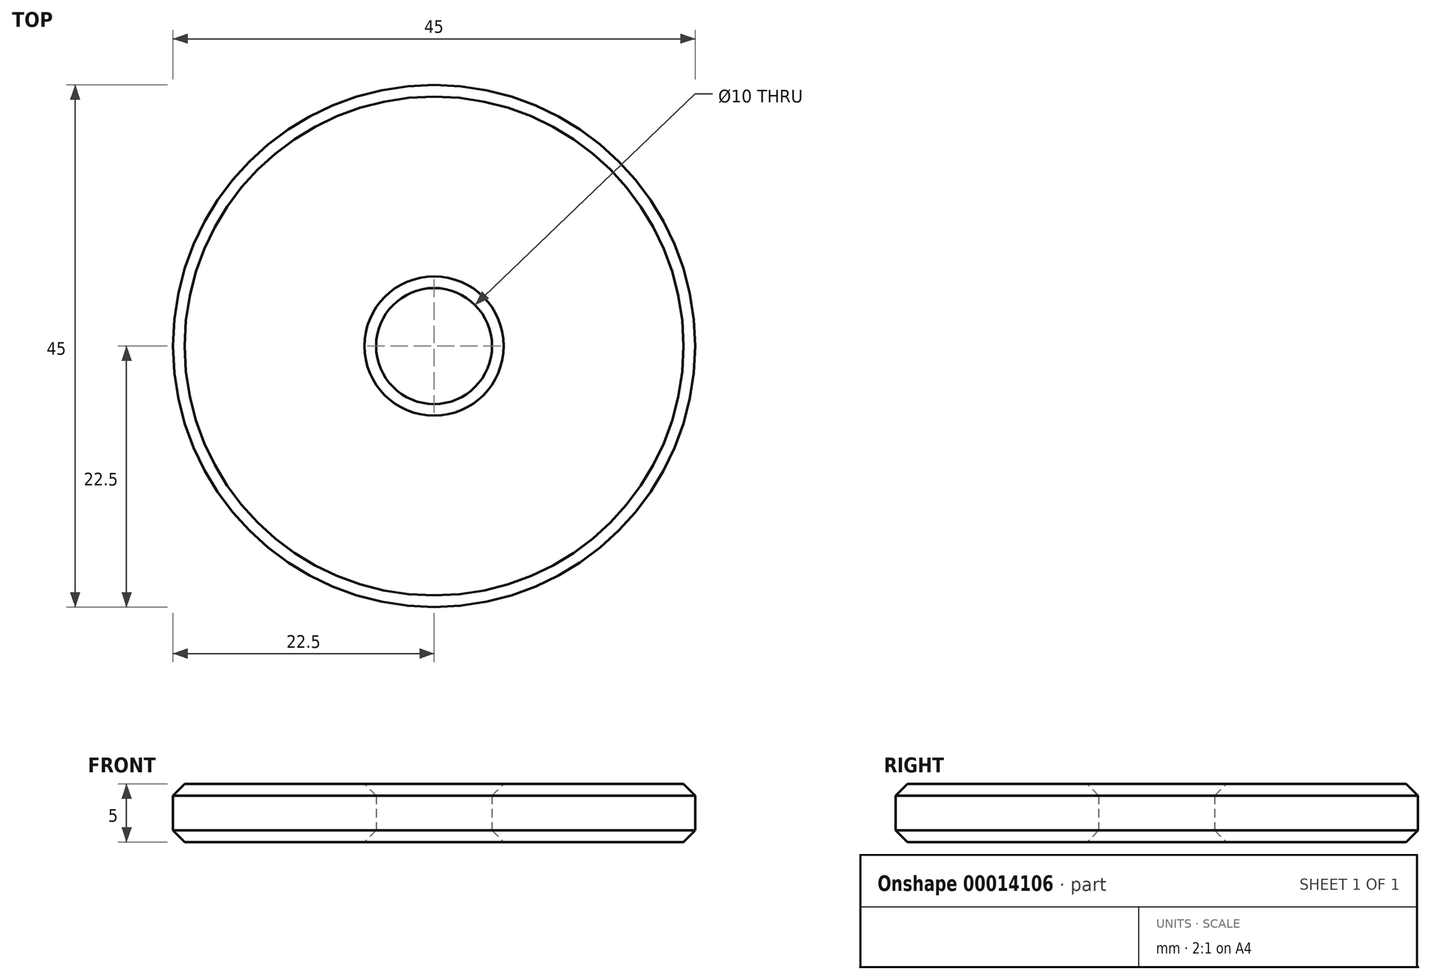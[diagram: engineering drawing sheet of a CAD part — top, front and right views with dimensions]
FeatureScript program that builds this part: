
annotation { "Feature Type Name" : "Feature", "Feature Type Description" : "" }
export const myFeature = defineFeature(function(context is Context, id is Id, definition is map)
    precondition{}
    {
        {
            var Q0;
            Q0=qCreatedBy(makeId("Top.planeOp"),FACE);
            var sketch = newSketch(context, id + "F0", { "sketchPlane" : qUnion([Q0])});
            skCircle(sketch, "E0", {"center": v(0, 0) * mm, "radius": 22.5 * mm});
            skCircle(sketch, "E1", {"center": v(0, 0) * mm, "radius": 5 * mm});
            skSolve(sketch);
        }
        {
            var Q0;
            Q0=qSketchRegion(id+"F0",true);
            extrude(context, id + "F1", {"entities" : qUnion([Q0]), "depth" : 5 * mm});
        }
        {
            var Q0;
            Q0=makeQuery(id+"F1.opExtrude","CAP_EDGE",EDGE,{"disambiguationData":[OSD([sQuery(id+"F0.wireOp",EDGE,"E0")])],"isStart":false});
            var Q1;
            Q1=makeQuery(id+"F1.opExtrude","CAP_EDGE",EDGE,{"disambiguationData":[OSD([sQuery(id+"F0.wireOp",EDGE,"E0")])],"isStart":true});
            var Q2;
            Q2=makeQuery(id+"F1.opExtrude","CAP_EDGE",EDGE,{"disambiguationData":[OSD([sQuery(id+"F0.wireOp",EDGE,"E1")])],"isStart":false});
            var Q3;
            Q3=makeQuery(id+"F1.opExtrude","CAP_EDGE",EDGE,{"disambiguationData":[OSD([sQuery(id+"F0.wireOp",EDGE,"E1")])],"isStart":true});
            chamfer(context, id + "F2", {"entities" : qUnion([Q0, Q1, Q2, Q3]), "width" : 1 * mm, "tangentPropagation" : true});
        }
    });
